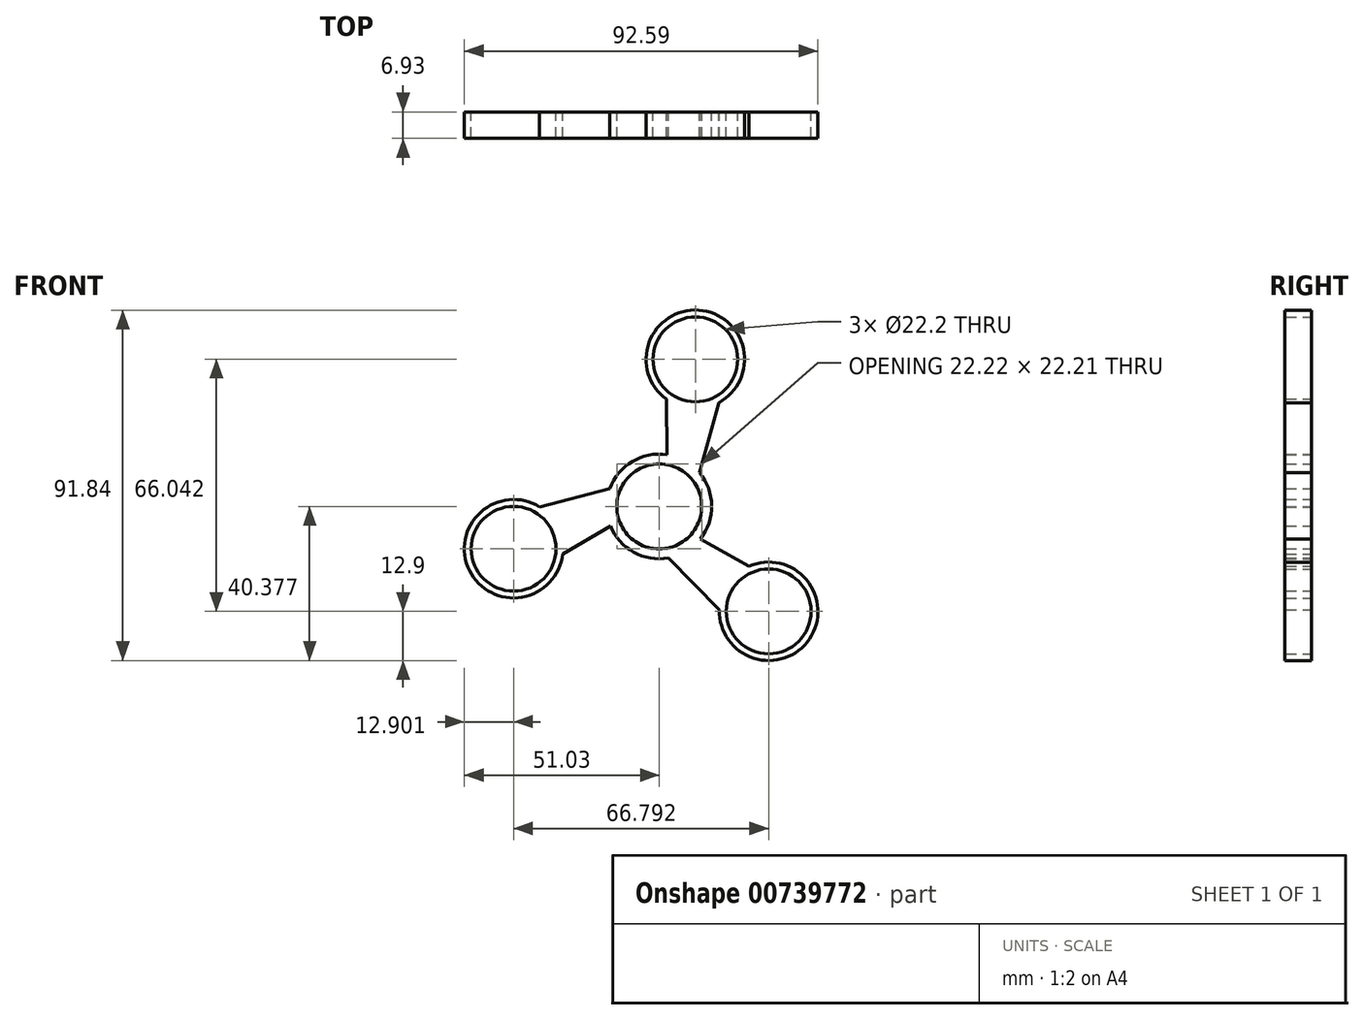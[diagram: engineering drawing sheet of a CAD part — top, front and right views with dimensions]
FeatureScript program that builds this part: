
annotation { "Feature Type Name" : "Feature", "Feature Type Description" : "" }
export const myFeature = defineFeature(function(context is Context, id is Id, definition is map)
    precondition{}
    {
        {
            var Q0;
            Q0=qCreatedBy(makeId("Front.planeOp"),FACE);
            var sketch = newSketch(context, id + "F0", { "sketchPlane" : qUnion([Q0])});
            skCircle(sketch, "E0", {"center": v(28.66, -27.48) * mm, "radius": 11.1 * mm});
            skCircle(sketch, "E1", {"center": v(0, -0.01) * mm, "radius": 11.1 * mm});
            skLineSegment(sketch, "E2", {"start": v(23.46, -15.67) * mm, "end": v(10.78, -8.5) * mm});
            skLineSegment(sketch, "E3", {"start": v(15.77, -27.1) * mm, "end": v(2.38, -13.53) * mm});
            skArc(sketch, "E4", {"start": v(10.78, -8.5) * mm, "mid": v(13.73, 0.2) * mm, "end": v(10.52, 8.83) * mm});
            skArc(sketch, "E5", {"start": v(15.77, -27.1) * mm, "mid": v(39.37, -34.68) * mm, "end": v(23.46, -15.67) * mm});
            skPoint(sketch, "E6.orphan", {"position": v(0, -11.11) * mm});
            skCircle(sketch, "E7.1.0", {"center": v(9.47, 38.56) * mm, "radius": 11.1 * mm});
            skLineSegment(sketch, "E7.1.1", {"start": v(15.6, 27.2) * mm, "end": v(10.52, 8.83) * mm});
            skLineSegment(sketch, "E7.1.2", {"start": v(1.84, 28.15) * mm, "end": v(1.98, 13.6) * mm});
            skArc(sketch, "E7.1.3", {"start": v(15.6, 27.2) * mm, "mid": v(10.35, 51.43) * mm, "end": v(1.84, 28.15) * mm});
            skCircle(sketch, "E7.1.4", {"center": v(0, 0) * mm, "radius": 11.1 * mm});
            skCircle(sketch, "E7.2.0", {"center": v(-38.13, -11.08) * mm, "radius": 11.1 * mm});
            skLineSegment(sketch, "E7.2.1", {"start": v(-31.36, -0.1) * mm, "end": v(-12.9, 4.7) * mm});
            skLineSegment(sketch, "E7.2.2", {"start": v(-25.3, -12.48) * mm, "end": v(-12.76, -5.08) * mm});
            skArc(sketch, "E7.2.3", {"start": v(-31.36, -0.1) * mm, "mid": v(-49.72, -16.75) * mm, "end": v(-25.3, -12.48) * mm});
            skCircle(sketch, "E7.2.4", {"center": v(0, 0) * mm, "radius": 11.1 * mm});
            skArc(sketch, "E8.trimOffspring", {"start": v(-12.76, -5.08) * mm, "mid": v(-6.7, -12) * mm, "end": v(2.38, -13.53) * mm});
            skArc(sketch, "E9.trimOffspring", {"start": v(1.98, 13.6) * mm, "mid": v(-7.04, 11.8) * mm, "end": v(-12.9, 4.7) * mm});
            skSolve(sketch);
        }
        {
            var Q0;
            Q0=makeQuery(id+"F0.imprint","IMPRINT",FACE,{"disambiguationData":[TD([[makeQuery(id+"F0.imprint","IMPRINT",EDGE,{"derivedFrom":sQuery(id+"F0.wireOp",EDGE,"E0")}),-1.0]])]});
            extrude(context, id + "F1", {"entities" : qUnion([Q0]), "depth" : 6.93 * mm, "offsetDistance" : 25.4 * mm});
        }
    });
